# Revit family: 1Electronics_Amplifier_Biamp_Commercial-Audio-Mixing-Amplifiers_MA120_MA240
name_source: partatom
category: Communication Devices
units: mm (PartAtom-declared; Revit-internal decimal feet)

## family parameters
Cut with Voids When Loaded = No
Host = Face
Maintain Annotation Orientation = No
OmniClass Number = 23.85.10.11.14
OmniClass Title = Audio Equipment
Part Type = Normal
Room Calculation Point = No
Round Connector Dimension = Use Diameter
Shared = No

## types (2) — shared parameters
Altitude = 0-6,600 ft (0-2000m) MSL
Compliance = FCC Part 15B (USA) UL listed (USA and Canada) CE Marked (Europe) RoHS Directive (Europe)
Connector Description = 100-240V/50-60Hz/180 W
Cooling = Convection
Default Elevation = 4' - 0"
Depth = 1' - 7"
Front Panel Indicators = Signal present, clipping, overload condition, emergency mode active, paging active, VOX active
Height = 0' - 3 1/2"
Housing Material = Biamp - Metal - Black
Humidity = 0-95% relative humidity (non-condensing)
Inputs 1-4 = -43 dBV (6 mVrms ± 10%)
Low Impedance Mode = Yes
Manufacturer = Biamp
Mic A, B (Balanced, VOX of) = -74 dBV (0.3 mVrms ± 10%)
Mic A, B (RCA) = -50 dBV (5 mVrms ± 10%)
Minimum Operational Load = 4Ω
Number of Output Channels = 1
Number of Poles = 1
Output Connectors = 4-pin, 0.3 inch (7.6 mm) Euroblock
Power Factor = 1
Product Documentation Link = https://downloads.biamp.com
Product Page URL = https://www.biamp.com
Product data url = https://www.bimobject.com
Protection = Temperature, overcurrent,overvoltage, undervoltage
SNR (1% THD) = > 90 dB
THD+N (@ -6dB) = < 0.5%
Temperature Range = 32 - 95° F (0 – 35° C)
Time to Auto Standby = 10 min
Topology = Class D
URL = https://www.biamp.com
Voltage = 120 V
Width = 1' - 0"

## per-type parameters (varying)
| type | Apparent Load | Description | Dynamic Power | Max Power Consumption | RMS Output Power (1% THD) | Weight |
| MA120 | 160 VA | MA120 120W Mixing Amplifier | 150 | 160 W | 120 | 11.02 lb |
| MA240 | 320 VA | MA240 240W Mixing Amplifier | 280 | 320 W | 240 | 13.23 lb |

note: column(s) folded — value = type name in every type: Model

## geometry (parser evidence)
native form markers: Sweep x7
no freeform markers — native parametric forms only
